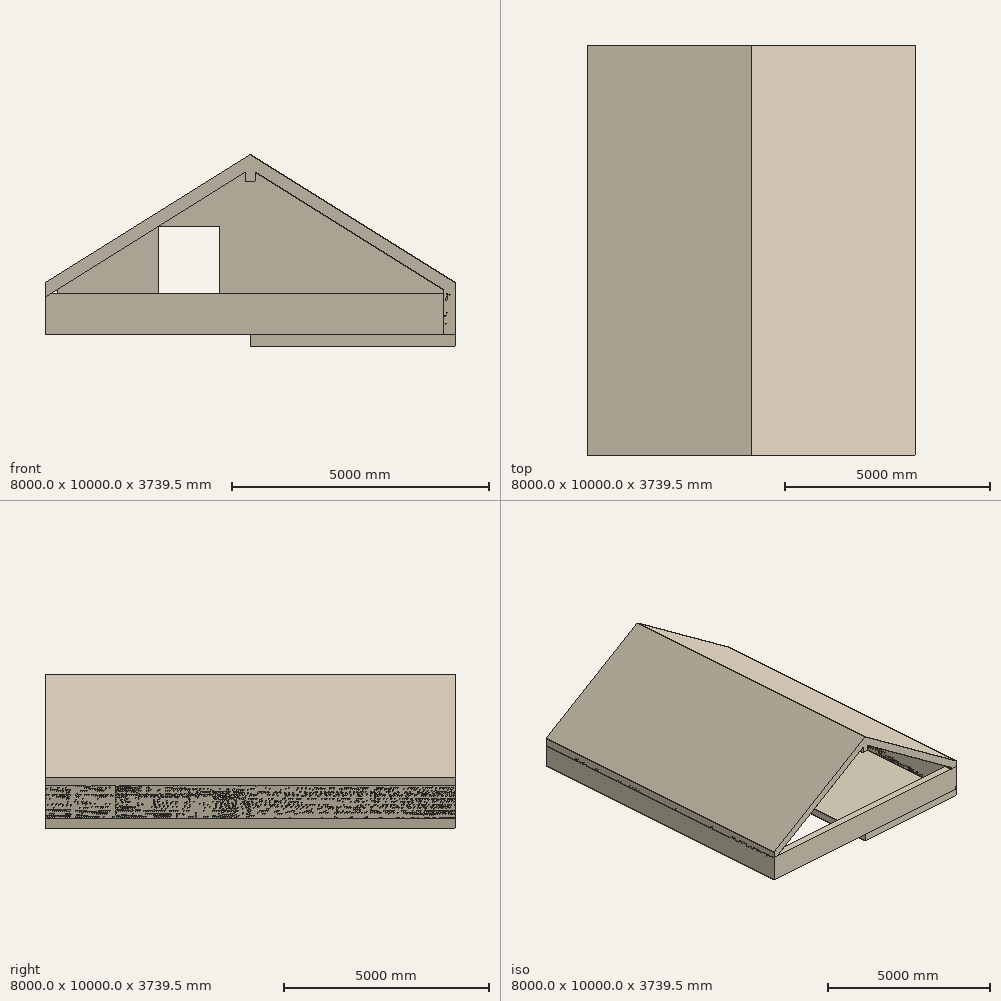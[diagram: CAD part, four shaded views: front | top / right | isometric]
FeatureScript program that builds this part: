
annotation { "Feature Type Name" : "Feature", "Feature Type Description" : "" }
export const myFeature = defineFeature(function(context is Context, id is Id, definition is map)
    precondition{}
    {
        {
            var Q0;
            Q0=qCreatedBy(makeId("Front.planeOp"),FACE);
            var sketch = newSketch(context, id + "F0", { "sketchPlane" : qUnion([Q0])});
            skLineSegment(sketch, "E0", {"start": v(0, 0) * mm, "end": v(-4000, 0) * mm});
            skLineSegment(sketch, "E1", {"start": v(-4000, 1000) * mm, "end": v(-4000, 0) * mm});
            skLineSegment(sketch, "E2", {"start": v(-4000, 1000) * mm, "end": v(0, 3499.48) * mm});
            skLineSegment(sketch, "E3.MirrorCS", {"start": v(0, 0) * mm, "end": v(4000, 0) * mm});
            skLineSegment(sketch, "E4.MirrorCS", {"start": v(4000, 1000) * mm, "end": v(4000, 0) * mm});
            skLineSegment(sketch, "E5.MirrorCS", {"start": v(4000, 1000) * mm, "end": v(0, 3499.48) * mm});
            skLineSegment(sketch, "E6", {"start": v(-4000, 0) * mm, "end": v(-3760, 0) * mm});
            skLineSegment(sketch, "E7", {"start": v(0, 3499.48) * mm, "end": v(0, 3216.47) * mm});
            skLineSegment(sketch, "E8", {"start": v(0, 3216.47) * mm, "end": v(-4000, 717) * mm});
            skPoint(sketch, "E8.endSnap0", {"position": v(-4000, 500) * mm});
            skLineSegment(sketch, "E9", {"start": v(-3760, 0) * mm, "end": v(-3760, 866.97) * mm});
            skLineSegment(sketch, "E10.MirrorCS", {"start": v(0, 3216.47) * mm, "end": v(4000, 717) * mm});
            skLineSegment(sketch, "E11.MirrorCS", {"start": v(3760, 0) * mm, "end": v(3760, 866.97) * mm});
            skLineSegment(sketch, "E12", {"start": v(0, 0) * mm, "end": v(0, -240) * mm});
            skLineSegment(sketch, "E13", {"start": v(0, -240) * mm, "end": v(-4000, -240) * mm});
            skLineSegment(sketch, "E14", {"start": v(-4000, -240) * mm, "end": v(-4000, 0) * mm});
            skLineSegment(sketch, "E15.MirrorCS", {"start": v(0, -240) * mm, "end": v(4000, -240) * mm});
            skLineSegment(sketch, "E16.MirrorCS", {"start": v(4000, -240) * mm, "end": v(4000, 0) * mm});
            skLineSegment(sketch, "E17.bottom", {"start": v(-100, 3216.47) * mm, "end": v(100, 3216.47) * mm});
            skLineSegment(sketch, "E17.top", {"start": v(-100, 2976.47) * mm, "end": v(100, 2976.47) * mm});
            skLineSegment(sketch, "E17.left", {"start": v(-100, 3216.47) * mm, "end": v(-100, 2976.47) * mm});
            skLineSegment(sketch, "E17.right", {"start": v(100, 3216.47) * mm, "end": v(100, 2976.47) * mm});
            skLineSegment(sketch, "E18", {"start": v(2746.93, 1500) * mm, "end": v(2746.93, 0) * mm});
            skLineSegment(sketch, "E19", {"start": v(-1800, 2091.7) * mm, "end": v(-1800, 0) * mm});
            skLineSegment(sketch, "E20", {"start": v(-600, 2841.55) * mm, "end": v(-600, 0) * mm});
            skLineSegment(sketch, "E21", {"start": v(-1800, 2091.7) * mm, "end": v(1800, 2091.7) * mm});
            skSolve(sketch);
        }
        {
            var Q0;
            Q0=qCreatedBy(makeId("Top.planeOp"),FACE);
            var sketch = newSketch(context, id + "F1", { "sketchPlane" : qUnion([Q0])});
            skLineSegment(sketch, "E22.bottom", {"start": v(-4000, 5000) * mm, "end": v(4000, 5000) * mm});
            skLineSegment(sketch, "E22.top", {"start": v(-4000, -5000) * mm, "end": v(4000, -5000) * mm});
            skLineSegment(sketch, "E22.left", {"start": v(-4000, 5000) * mm, "end": v(-4000, -5000) * mm});
            skLineSegment(sketch, "E22.right", {"start": v(4000, 5000) * mm, "end": v(4000, -5000) * mm});
            skPoint(sketch, "E22.middle", {"position": v(0, 0) * mm});
            skLineSegment(sketch, "E23.bottom", {"start": v(3760, 4760) * mm, "end": v(-3760, 4760) * mm});
            skLineSegment(sketch, "E23.top", {"start": v(3760, -4760) * mm, "end": v(-3760, -4760) * mm});
            skLineSegment(sketch, "E23.left", {"start": v(3760, 4760) * mm, "end": v(3760, -4760) * mm});
            skLineSegment(sketch, "E23.right", {"start": v(-3760, 4760) * mm, "end": v(-3760, -4760) * mm});
            skSolve(sketch);
        }
        {
            var Q0;
            Q0=makeQuery(id+"F1.imprint","IMPRINT",FACE,{"disambiguationData":[TD([[makeQuery(id+"F1.imprint","IMPRINT",EDGE,{"derivedFrom":sQuery(id+"F1.wireOp",EDGE,"E22.bottom")}),-1.0]])]});
            extrude(context, id + "F2", {"entities" : qUnion([Q0]), "depth" : 800 * mm, "offsetDistance" : 25 * mm});
        }
        {
            var Q0;
            {var subQ0=sQuery(id+"F0.wireOp",EDGE,"E6");Q0=makeQuery(id+"F0.imprint","IMPRINT",FACE,{"disambiguationData":[TD([[makeQuery(id+"F0.imprint","IMPRINT",EDGE,{"derivedFrom":subQ0}),-1.0]])]});}
            var Q1;
            {var subQ4=sQuery(id+"F0.wireOp",EDGE,"E12");Q1=makeQuery(id+"F0.imprint","IMPRINT",FACE,{"disambiguationData":[TD([[makeQuery(id+"F0.imprint","IMPRINT",EDGE,{"derivedFrom":subQ4}),1.0]])]});}
            extrude(context, id + "F3", {"entities" : qUnion([Q0, Q1]), "endBound" : BoundingType.SYMMETRIC, "depth" : 10000 * mm, "offsetDistance" : 25 * mm});
        }
        {
            var Q0;
            {var subQ4=sQuery(id+"F0.wireOp",EDGE,"E2");Q0=makeQuery(id+"F0.imprint","IMPRINT",FACE,{"disambiguationData":[TD([[makeQuery(id+"F0.imprint","IMPRINT",EDGE,{"derivedFrom":subQ4}),-1.0]])]});}
            var Q1;
            {var subQ10=sQuery(id+"F0.wireOp",EDGE,"E5.MirrorCS");Q1=makeQuery(id+"F0.imprint","IMPRINT",FACE,{"disambiguationData":[TD([[makeQuery(id+"F0.imprint","IMPRINT",EDGE,{"derivedFrom":subQ10}),1.0]])]});}
            var Q2;
            {var subQ0=sQuery(id+"F0.wireOp",EDGE,"E6");Q2=makeQuery(id+"F0.imprint","IMPRINT",FACE,{"disambiguationData":[TD([[makeQuery(id+"F0.imprint","IMPRINT",EDGE,{"derivedFrom":subQ0}),1.0]])]});}
            var Q3;
            {var subQ3=sQuery(id+"F0.wireOp",EDGE,"E11.MirrorCS");Q3=makeQuery(id+"F0.imprint","IMPRINT",FACE,{"disambiguationData":[TD([[makeQuery(id+"F0.imprint","IMPRINT",EDGE,{"derivedFrom":subQ3}),-1.0]])]});}
            var Q4;
            {var subQ0=sQuery(id+"F0.wireOp",EDGE,"E17.top");Q4=makeQuery(id+"F0.imprint","IMPRINT",FACE,{"disambiguationData":[TD([[makeQuery(id+"F0.imprint","IMPRINT",EDGE,{"derivedFrom":subQ0}),1.0]])]});}
            var Q5;
            {var subQ0=sQuery(id+"F0.wireOp",EDGE,"E17.bottom");var subQ3=sQuery(id+"F0.wireOp",EDGE,"E17.left");var subQ5=makeQuery(id+"F0.imprint","INTERSECT",VERTEX,{"derivedFrom":[subQ0,subQ3]});Q5=makeQuery(id+"F0.imprint","IMPRINT",FACE,{"disambiguationData":[TD([[makeQuery(id+"F0.imprint","IMPRINT",EDGE,{"disambiguationData":[TD([[subQ5,-1.0]])],"derivedFrom":subQ3}),1.0]])]});}
            var Q6;
            {var subQ0=sQuery(id+"F0.wireOp",EDGE,"E17.bottom");var subQ3=sQuery(id+"F0.wireOp",EDGE,"E17.right");var subQ5=makeQuery(id+"F0.imprint","INTERSECT",VERTEX,{"derivedFrom":[subQ0,subQ3]});Q6=makeQuery(id+"F0.imprint","IMPRINT",FACE,{"disambiguationData":[TD([[makeQuery(id+"F0.imprint","IMPRINT",EDGE,{"disambiguationData":[TD([[subQ5,-1.0]])],"derivedFrom":subQ3}),-1.0]])]});}
            extrude(context, id + "F4", {"entities" : qUnion([Q0, Q1, Q2, Q3, Q4, Q5, Q6]), "endBound" : BoundingType.SYMMETRIC, "depth" : 10000 * mm, "offsetDistance" : 25 * mm});
        }
        {
            var Q0;
            {var subQ1=sQuery(id+"F0.wireOp",EDGE,"E8");var subQ3=sQuery(id+"F0.wireOp",EDGE,"E20");var subQ4=makeQuery(id+"F0.imprint","INTERSECT",VERTEX,{"derivedFrom":[subQ1,subQ3]});Q0=makeQuery(id+"F0.imprint","IMPRINT",FACE,{"disambiguationData":[TD([[makeQuery(id+"F0.imprint","IMPRINT",EDGE,{"disambiguationData":[TD([[subQ4,-1.0]])],"derivedFrom":subQ3}),-1.0]])]});}
            var Q1;
            {var subQ0=sQuery(id+"F0.wireOp",EDGE,"E17.top");Q1=makeQuery(id+"F0.imprint","IMPRINT",FACE,{"disambiguationData":[TD([[makeQuery(id+"F0.imprint","IMPRINT",EDGE,{"derivedFrom":subQ0}),-1.0]])]});}
            var Q2;
            {var subQ0=sQuery(id+"F0.wireOp",EDGE,"E18");Q2=makeQuery(id+"F0.imprint","IMPRINT",FACE,{"disambiguationData":[TD([[makeQuery(id+"F0.imprint","IMPRINT",EDGE,{"derivedFrom":subQ0}),-1.0]])]});}
            var Q3;
            {var subQ0=sQuery(id+"F0.wireOp",EDGE,"E11.MirrorCS");Q3=makeQuery(id+"F0.imprint","IMPRINT",FACE,{"disambiguationData":[TD([[makeQuery(id+"F0.imprint","IMPRINT",EDGE,{"derivedFrom":subQ0}),1.0]])]});}
            var Q4;
            {var subQ0=sQuery(id+"F0.wireOp",EDGE,"E9");Q4=makeQuery(id+"F0.imprint","IMPRINT",FACE,{"disambiguationData":[TD([[makeQuery(id+"F0.imprint","IMPRINT",EDGE,{"derivedFrom":subQ0}),-1.0]])]});}
            extrude(context, id + "F5", {"entities" : qUnion([Q0, Q1, Q2, Q3, Q4]), "endBound" : BoundingType.SYMMETRIC, "depth" : 110 * mm, "offsetDistance" : 25 * mm});
        }
    });
